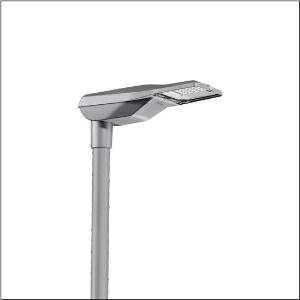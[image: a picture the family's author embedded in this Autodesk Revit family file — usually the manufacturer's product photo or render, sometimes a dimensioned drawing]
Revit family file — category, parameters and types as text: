
# Revit family: streetlight_sl_21_iq_micro___st1_0a_5xe1d41d08db_a30f
name_source: partatom
category: Lighting Fixtures
units: mm (PartAtom-declared; Revit-internal decimal feet)

## family parameters
Cut with Voids When Loaded = No
Host = Face
Light Source = No
Part Type = Normal
Room Calculation Point = No
Round Connector Dimension = Use Diameter
Shared = No

## types (1)
- --- (1 x LED, 5010 lm, 36.4 W, 4000K)
    Apparent Load = 36 VA
    CIE Flux Codes = 37 72 97 100 100
    Color Rendering = 70
    Color Temperature = 4000K
    Default Elevation = 1800 mm
    Description = Streetlight SL 21 iQ micro, mast luminaire, primary light control with lens, of PMMA, primary optical cover: cover, of toughened safety glass, transparent, light distribution: ST1.0a, light emission: direct distribution, primary light characteristic: asymmetric, installation type: post-top, side-entry, LED, High Power LED, rated luminous flux: 5.010lm, luminous efficacy: 138lm/W, light colour: 740, colour temperature: 4000K, control: Auto-Match, Temp-Guard, Lumen-Switch, Night-Set, Smart-Wire, Light-Fading, Desk-Remote (wireless, voltage-free reading and setting of iQ features in the workshop via application-optimized NFC function/RFID function), optimised constant luminous flux control (CLO 2.0), presetting dimming linear, mains connection: 220..240V, AC, 50/60Hz, start of lifetime: 36W, end of service life: 38W, reduction: 16W, luminaire housing, of diecast aluminium, powder-coated, Siteco® metallic grey (DB 702S), corrosivity category C5 mid according to DIN EN ISO 12944, please order mast flange separately, inclination adjustable: 0°, 5°, 10°, 15°, sealing non-destructively replaceable, multi-level sealing system, length: 528mm, width: 235mm, height: 110mm, mast flange for spigot size: 42mm (side-entry): 5XC10008XM4, 60/48mm (side-entry/post-top): 5XC10108XM2, 76/60mm (side-entry/post-top): 5XC10108XM1, protection rating (complete): IP66, insulation class (complete): insulation class II (safety insulation), certification: CE, ENEC, ENEC+, VDE, impact resistance: IK09, permissible operating ambient temperature for outdoor applications: -40..+50°C, standard-compliant lighting for roads and squares, packaging unit: 1 piece

Light Distribution: ST1.0a
    Height = 110 mm
    Lamp = 1 x LED
    Lamp Light Flux = 5010 lm
    Lamp Power = 36.4 W
    Lamp count = 1
    Length = 528 mm
    Luminous efficacy = 138 lm/W
    Manufacturer = Siteco
    ModVariant = No
    Model = 5XE1D41D08DB
    Number of Poles = 1
    OnlyDefault = Yes
    Power Factor = 1
    Product Name = Streetlight SL 21 iQ micro | ST1.0a
    Product group = mast luminaire | pylon top
    ProductGroupID = 6100
    Protection Class = Protection class II
    Protection Degree = IP 66
    RLX_Detail_Level = 1
    RLX_Emergency_Light_Flux = 0 lm
    RLX_Emergency_Type = 0
    RLX_Emergency_Type_DB = No
    RlxData = <blob elided: 99553 chars, md5=8a74815d>
    Socket = socket
    Standby Power = 0 W
    System Light Flux = 5010 lm
    System Power = 36 W
    Type Comments = factory setting: luminous flux: 100 % | dim-lin: 254 | 715 mA
    Type Image = l_1006881.jpg
    URL = http://relux.com
    VarID = @adj_088253
    Voltage = 0 V
    Weight = 0.00 kg
    Width = 235 mm

## geometry (parser evidence)
native form markers: Blend x4, Sweep x9
no freeform markers — native parametric forms only
